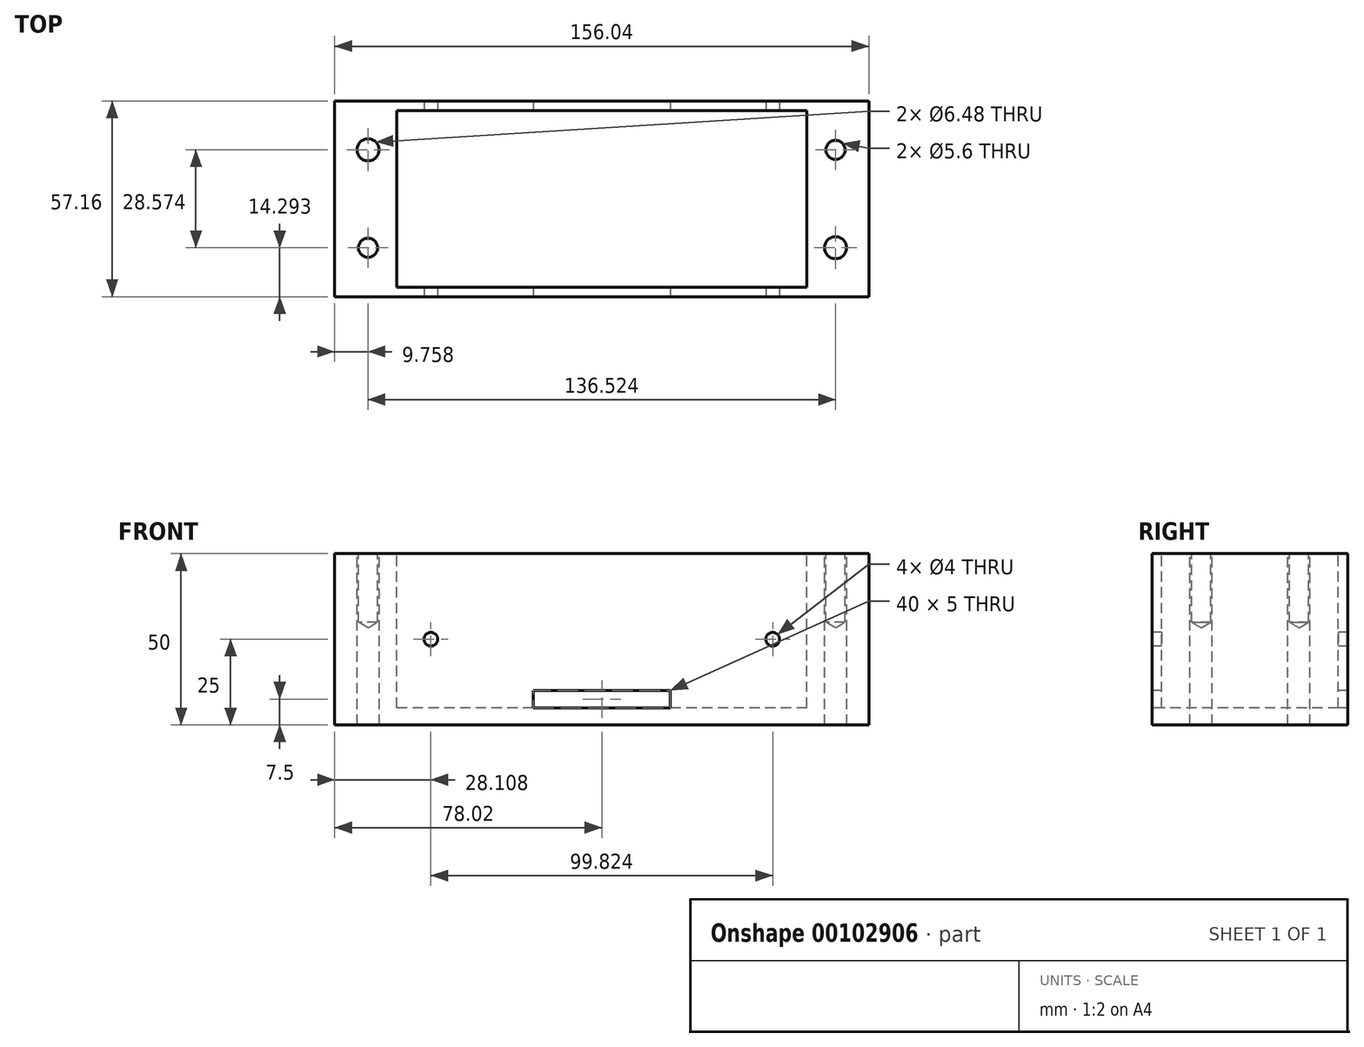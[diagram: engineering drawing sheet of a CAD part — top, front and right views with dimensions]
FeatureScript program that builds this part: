
annotation { "Feature Type Name" : "Feature", "Feature Type Description" : "" }
export const myFeature = defineFeature(function(context is Context, id is Id, definition is map)
    precondition{}
    {
        {
            var Q0;
            Q0=qCreatedBy(makeId("Top.planeOp"),FACE);
            var sketch = newSketch(context, id + "F0", { "sketchPlane" : qUnion([Q0])});
            skLineSegment(sketch, "E0", {"start": v(-68.26, 20.64) * mm, "end": v(-72.23, 20.64) * mm});
            skLineSegment(sketch, "E1", {"start": v(-72.23, 20.64) * mm, "end": v(-72.23, 27.78) * mm});
            skArc(sketch, "E2", {"start": v(-68.26, 7.94) * mm, "mid": v(-61.91, 14.29) * mm, "end": v(-68.26, 20.64) * mm});
            skLineSegment(sketch, "E3", {"start": v(-68.26, 7.94) * mm, "end": v(-72.23, 7.94) * mm});
            skLineSegment(sketch, "E4", {"start": v(-72.23, -7.94) * mm, "end": v(-72.23, 7.94) * mm});
            skLineSegment(sketch, "E5", {"start": v(72.22, 20.64) * mm, "end": v(72.22, 27.78) * mm});
            skLineSegment(sketch, "E6", {"start": v(72.22, 27.78) * mm, "end": v(-72.22, 27.78) * mm});
            skLineSegment(sketch, "E7", {"start": v(72.22, -7.94) * mm, "end": v(72.22, 7.94) * mm});
            skArc(sketch, "E8", {"start": v(68.18, -7.94) * mm, "mid": v(61.91, -14.37) * mm, "end": v(68.35, -20.64) * mm});
            skLineSegment(sketch, "E9", {"start": v(68.18, -7.94) * mm, "end": v(72.22, -7.94) * mm});
            skLineSegment(sketch, "E10", {"start": v(72.22, -27.78) * mm, "end": v(72.22, -20.64) * mm});
            skLineSegment(sketch, "E11", {"start": v(68.35, -20.64) * mm, "end": v(72.22, -20.64) * mm});
            skLineSegment(sketch, "E12", {"start": v(-72.23, -27.78) * mm, "end": v(-72.23, -20.64) * mm});
            skLineSegment(sketch, "E13", {"start": v(-72.23, -27.78) * mm, "end": v(72.22, -27.78) * mm});
            skCircle(sketch, "E14", {"center": v(68.26, -14.29) * mm, "radius": 3.24 * mm});
            skCircle(sketch, "E15", {"center": v(-68.26, 14.29) * mm, "radius": 3.24 * mm});
            skLineSegment(sketch, "E16", {"start": v(-73.03, 28.57) * mm, "end": v(73.02, 28.57) * mm});
            skLineSegment(sketch, "E17", {"start": v(-73.03, -28.57) * mm, "end": v(-73.03, 28.57) * mm});
            skLineSegment(sketch, "E18", {"start": v(73.03, -28.57) * mm, "end": v(-73.02, -28.57) * mm});
            skLineSegment(sketch, "E19", {"start": v(73.03, 28.57) * mm, "end": v(73.03, -28.57) * mm});
            skCircle(sketch, "E20.MirrorC", {"center": v(68.26, 14.29) * mm, "radius": 3.24 * mm});
            skArc(sketch, "E21.MirrorCS", {"start": v(68.26, 7.94) * mm, "mid": v(61.91, 14.29) * mm, "end": v(68.26, 20.64) * mm});
            skLineSegment(sketch, "E22.MirrorCS", {"start": v(68.26, 20.64) * mm, "end": v(72.23, 20.64) * mm});
            skLineSegment(sketch, "E23.MirrorCS", {"start": v(68.26, 7.94) * mm, "end": v(72.23, 7.94) * mm});
            skLineSegment(sketch, "E24.MirrorCS", {"start": v(-68.26, -20.64) * mm, "end": v(-72.23, -20.64) * mm});
            skArc(sketch, "E25.MirrorCS", {"start": v(-68.26, -7.94) * mm, "mid": v(-61.91, -14.29) * mm, "end": v(-68.26, -20.64) * mm});
            skCircle(sketch, "E26.MirrorC", {"center": v(-68.26, -14.29) * mm, "radius": 3.24 * mm});
            skLineSegment(sketch, "E27.MirrorCS", {"start": v(-68.26, -7.94) * mm, "end": v(-72.23, -7.94) * mm});
            skLineSegment(sketch, "E28.bottom", {"start": v(73.02, 28.57) * mm, "end": v(78.02, 28.57) * mm});
            skLineSegment(sketch, "E28.top", {"start": v(73.02, -28.57) * mm, "end": v(78.02, -28.57) * mm});
            skLineSegment(sketch, "E28.left", {"start": v(73.02, 28.57) * mm, "end": v(73.02, -28.57) * mm});
            skLineSegment(sketch, "E28.right", {"start": v(78.02, 28.57) * mm, "end": v(78.02, -28.57) * mm});
            skLineSegment(sketch, "E29.MirrorCS", {"start": v(-73.02, -28.57) * mm, "end": v(-78.02, -28.57) * mm});
            skLineSegment(sketch, "E30.MirrorCS", {"start": v(-78.02, 28.57) * mm, "end": v(-78.02, -28.57) * mm});
            skLineSegment(sketch, "E31.MirrorCS", {"start": v(-73.02, 28.57) * mm, "end": v(-78.02, 28.57) * mm});
            skSolve(sketch);
        }
        {
            var Q0;
            Q0 = qSketchRegion(id + "F0", true);
            var Q1;
            Q1=makeQuery(id+"F0.imprint","IMPRINT",FACE,{"disambiguationData":[TD([[makeQuery(id+"F0.imprint","IMPRINT",EDGE,{"derivedFrom":sQuery(id+"F0.wireOp",EDGE,"E15")}),-1.0]])]});
            var Q2;
            Q2=makeQuery(id+"F0.imprint","IMPRINT",FACE,{"disambiguationData":[TD([[makeQuery(id+"F0.imprint","IMPRINT",EDGE,{"derivedFrom":sQuery(id+"F0.wireOp",EDGE,"E2")}),-1.0]])]});
            var Q3;
            Q3=makeQuery(id+"F0.imprint","IMPRINT",FACE,{"disambiguationData":[TD([[makeQuery(id+"F0.imprint","IMPRINT",EDGE,{"derivedFrom":sQuery(id+"F0.wireOp",EDGE,"E26.MirrorC")}),1.0]])]});
            var Q4;
            Q4=makeQuery(id+"F0.imprint","IMPRINT",FACE,{"disambiguationData":[TD([[makeQuery(id+"F0.imprint","IMPRINT",EDGE,{"derivedFrom":sQuery(id+"F0.wireOp",EDGE,"E20.MirrorC")}),1.0]])]});
            var Q5;
            Q5=makeQuery(id+"F0.imprint","IMPRINT",FACE,{"disambiguationData":[TD([[makeQuery(id+"F0.imprint","IMPRINT",EDGE,{"derivedFrom":sQuery(id+"F0.wireOp",EDGE,"E14")}),-1.0]])]});
            extrude(context, id + "F1", {"entities" : qUnion([Q0, Q1, Q2, Q3, Q4, Q5]), "oppositeDirection" : true, "depth" : 50 * mm});
        }
        {
            var Q0;
            Q0=makeQuery(id+"F1.opExtrude","CAP_FACE",FACE,{"disambiguationData":[OSD([sQuery(id+"F0.wireOp",EDGE,"E16"),sQuery(id+"F0.wireOp",EDGE,"E18"),sQuery(id+"F0.wireOp",EDGE,"E28.bottom"),sQuery(id+"F0.wireOp",EDGE,"E28.top"),sQuery(id+"F0.wireOp",EDGE,"E28.right"),sQuery(id+"F0.wireOp",EDGE,"E29.MirrorCS"),sQuery(id+"F0.wireOp",EDGE,"E30.MirrorCS"),sQuery(id+"F0.wireOp",EDGE,"E31.MirrorCS")])],"isStart":true});
            var sketch = newSketch(context, id + "F2", { "sketchPlane" : qUnion([Q0])});
            skLineSegment(sketch, "E32.bottom", {"start": v(59.91, 25.78) * mm, "end": v(-59.91, 25.78) * mm});
            skLineSegment(sketch, "E32.top", {"start": v(59.91, -25.78) * mm, "end": v(-59.91, -25.78) * mm});
            skLineSegment(sketch, "E32.left", {"start": v(59.91, 25.78) * mm, "end": v(59.91, -25.78) * mm});
            skLineSegment(sketch, "E32.right", {"start": v(-59.91, 25.78) * mm, "end": v(-59.91, -25.78) * mm});
            skPoint(sketch, "E32.middle", {"position": v(0, 0) * mm});
            skSolve(sketch);
        }
        {
            var Q0;
            Q0 = qSketchRegion(id + "F2", true);
            extrude(context, id + "F3", {"entities" : qUnion([Q0]), "operationType" : NewBodyOperationType.REMOVE, "oppositeDirection" : true, "depth" : 45 * mm});
        }
        {
            var Q0;
            Q0=sQuery(id+"F0.wireOp",VERTEX,"E2.center");
            var Q1;
            Q1=sQuery(id+"F0.wireOp",VERTEX,"E25.MirrorCS.center");
            var Q2;
            Q2=sQuery(id+"F0.wireOp",VERTEX,"E20.MirrorC.center");
            var Q3;
            Q3=sQuery(id+"F0.wireOp",VERTEX,"E8.center");
            var Q4;
            Q4=makeQuery(id+"F1.opExtrude","SWEPT_BODY",BODY,{"disambiguationData":[OSD([sQuery(id+"F0.wireOp",EDGE,"E16"),sQuery(id+"F0.wireOp",EDGE,"E18"),sQuery(id+"F0.wireOp",EDGE,"E28.bottom"),sQuery(id+"F0.wireOp",EDGE,"E28.top"),sQuery(id+"F0.wireOp",EDGE,"E28.right"),sQuery(id+"F0.wireOp",EDGE,"E29.MirrorCS"),sQuery(id+"F0.wireOp",EDGE,"E30.MirrorCS"),sQuery(id+"F0.wireOp",EDGE,"E31.MirrorCS")])]});
            hole(context, id + "F4", {"style" : HoleStyle.SIMPLE, "endStyle" : HoleEndStyle.BLIND, "holeDiameter" : 5.6 * mm, "holeDepth" : 20 * mm, "locations" : qUnion([Q0, Q1, Q2, Q3]), "scope" : qUnion([Q4])});
        }
        {
            var Q0;
            Q0=makeQuery(id+"F1.opExtrude","SWEPT_FACE",FACE,{"disambiguationData":[OSD([sQuery(id+"F0.wireOp",EDGE,"E18"),sQuery(id+"F0.wireOp",EDGE,"E28.top"),sQuery(id+"F0.wireOp",EDGE,"E29.MirrorCS")])]});
            var sketch = newSketch(context, id + "F5", { "sketchPlane" : qUnion([Q0])});
            skLineSegment(sketch, "E33.bottom", {"start": v(20, -40) * mm, "end": v(-20, -40) * mm});
            skLineSegment(sketch, "E33.top", {"start": v(20, -45) * mm, "end": v(-20, -45) * mm});
            skLineSegment(sketch, "E33.left", {"start": v(20, -40) * mm, "end": v(20, -45) * mm});
            skLineSegment(sketch, "E33.right", {"start": v(-20, -40) * mm, "end": v(-20, -45) * mm});
            skPoint(sketch, "E33.middle", {"position": v(0, -42.5) * mm});
            skPoint(sketch, "E34", {"position": v(-49.91, -25) * mm});
            skPoint(sketch, "E35.MirrorP", {"position": v(49.91, -25) * mm});
            skSolve(sketch);
        }
        {
            var Q0;
            Q0 = qSketchRegion(id + "F5", true);
            extrude(context, id + "F6", {"entities" : qUnion([Q0]), "operationType" : NewBodyOperationType.REMOVE, "endBound" : BoundingType.THROUGH_ALL, "oppositeDirection" : true, "depth" : 25 * mm});
        }
        {
            var Q0;
            Q0=sQuery(id+"F5.wireOp",VERTEX,"E34");
            var Q1;
            Q1=sQuery(id+"F5.wireOp",VERTEX,"E35.MirrorP");
            var Q2;
            Q2=makeQuery(id+"F1.opExtrude","SWEPT_BODY",BODY,{"disambiguationData":[OSD([sQuery(id+"F0.wireOp",EDGE,"E16"),sQuery(id+"F0.wireOp",EDGE,"E18"),sQuery(id+"F0.wireOp",EDGE,"E28.bottom"),sQuery(id+"F0.wireOp",EDGE,"E28.top"),sQuery(id+"F0.wireOp",EDGE,"E28.right"),sQuery(id+"F0.wireOp",EDGE,"E29.MirrorCS"),sQuery(id+"F0.wireOp",EDGE,"E30.MirrorCS"),sQuery(id+"F0.wireOp",EDGE,"E31.MirrorCS")])]});
            hole(context, id + "F7", {"style" : HoleStyle.SIMPLE, "endStyle" : HoleEndStyle.THROUGH, "holeDiameter" : 4 * mm, "locations" : qUnion([Q0, Q1]), "scope" : qUnion([Q2]), "isTappedThrough" : true});
        }
    });
